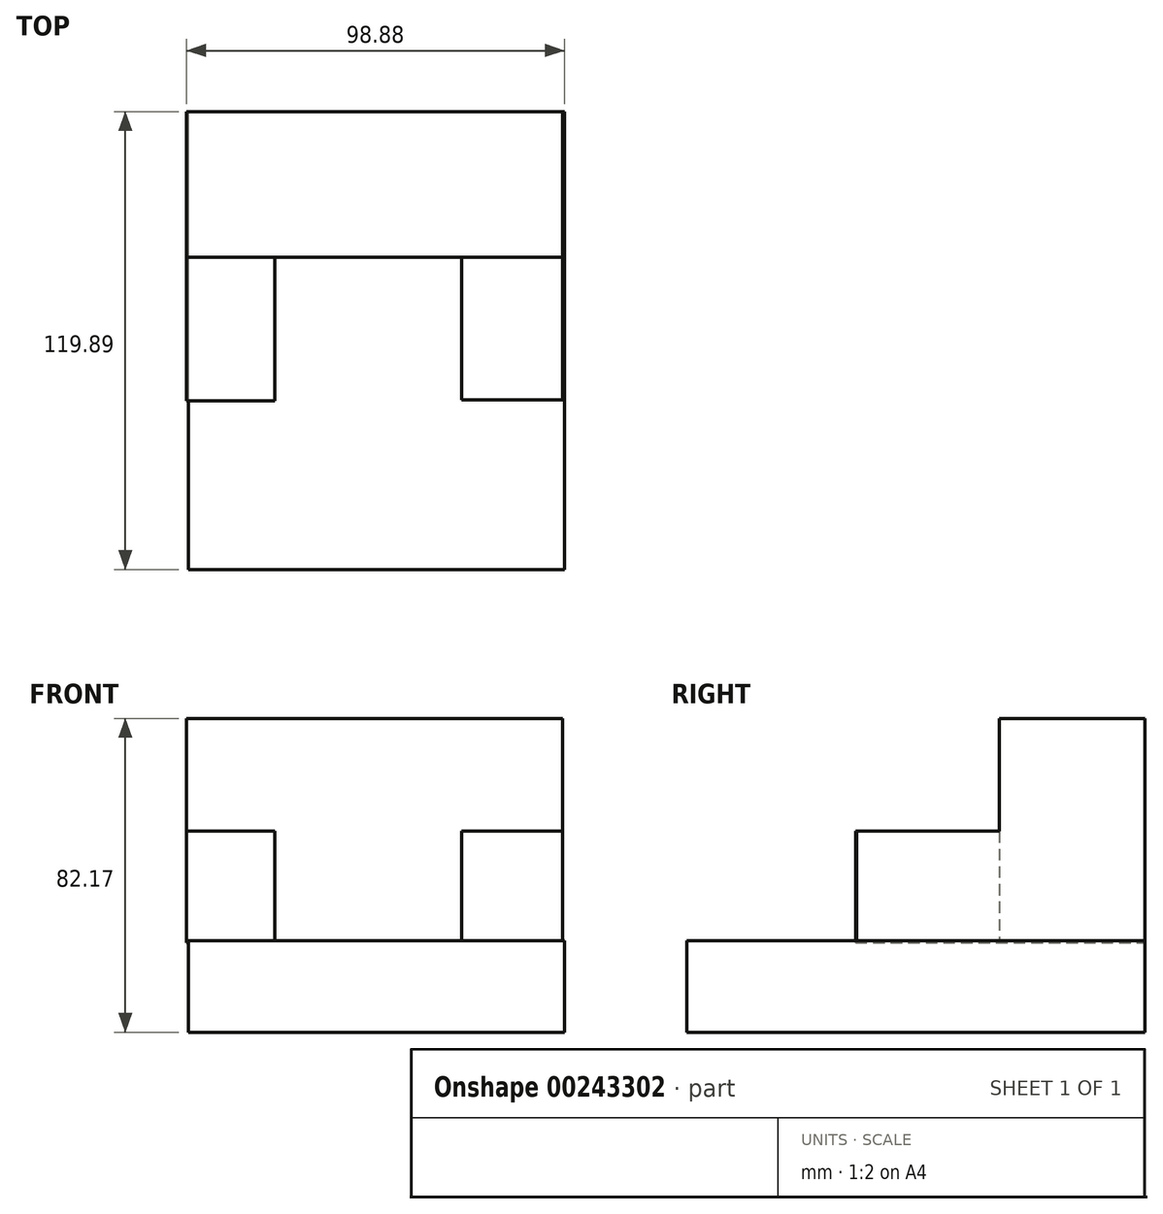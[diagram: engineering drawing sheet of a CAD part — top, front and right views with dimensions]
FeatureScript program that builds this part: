
annotation { "Feature Type Name" : "Feature", "Feature Type Description" : "" }
export const myFeature = defineFeature(function(context is Context, id is Id, definition is map)
    precondition{}
    {
        {
            var Q0;
            Q0=qCreatedBy(makeId("Front.planeOp"),FACE);
            var sketch = newSketch(context, id + "F0", { "sketchPlane" : qUnion([Q0])});
            skLineSegment(sketch, "E0.bottom", {"start": v(-49.67, 29.57) * mm, "end": v(48.76, 29.57) * mm});
            skLineSegment(sketch, "E0.top", {"start": v(-49.67, -29.12) * mm, "end": v(48.76, -29.12) * mm});
            skLineSegment(sketch, "E0.left", {"start": v(-49.67, 29.57) * mm, "end": v(-49.67, -29.12) * mm});
            skLineSegment(sketch, "E0.right", {"start": v(48.76, 29.57) * mm, "end": v(48.76, -29.12) * mm});
            skPoint(sketch, "E0.middle", {"position": v(-0.45, 0.23) * mm});
            skSolve(sketch);
        }
        {
            var Q0;
            Q0=makeQuery(id+"F0.imprint","IMPRINT",FACE,{"disambiguationData":[TD([[makeQuery(id+"F0.imprint","IMPRINT",EDGE,{"derivedFrom":sQuery(id+"F0.wireOp",EDGE,"E0.bottom")}),-1.0]])]});
            extrude(context, id + "F1", {"entities" : qUnion([Q0]), "depth" : 38.1 * mm});
        }
        {
            var Q0;
            Q0=makeQuery(id+"F1.opExtrude","CAP_FACE",FACE,{"disambiguationData":[OSD([sQuery(id+"F0.wireOp",EDGE,"E0.bottom"),sQuery(id+"F0.wireOp",EDGE,"E0.top"),sQuery(id+"F0.wireOp",EDGE,"E0.left"),sQuery(id+"F0.wireOp",EDGE,"E0.right")])],"isStart":false});
            var sketch = newSketch(context, id + "F2", { "sketchPlane" : qUnion([Q0])});
            skPoint(sketch, "E1.firstSnap0", {"position": v(-49.67, 0.23) * mm});
            skLineSegment(sketch, "E1.bottom", {"start": v(-49.67, 0) * mm, "end": v(-26.64, 0) * mm});
            skLineSegment(sketch, "E1.top", {"start": v(-49.67, -29.12) * mm, "end": v(-26.64, -29.12) * mm});
            skLineSegment(sketch, "E1.left", {"start": v(-49.67, 0) * mm, "end": v(-49.67, -29.12) * mm});
            skLineSegment(sketch, "E1.right", {"start": v(-26.64, 0) * mm, "end": v(-26.64, -29.12) * mm});
            skSolve(sketch);
        }
        {
            var Q0;
            Q0=makeQuery(id+"F2.imprint","IMPRINT",FACE,{"disambiguationData":[TD([[makeQuery(id+"F2.imprint","IMPRINT",EDGE,{"derivedFrom":sQuery(id+"F2.wireOp",EDGE,"E1.bottom")}),-1.0]])]});
            extrude(context, id + "F3", {"entities" : qUnion([Q0]), "operationType" : NewBodyOperationType.ADD, "depth" : 37.6 * mm});
        }
        {
            var Q0;
            Q0=makeQuery(id+"F1.opExtrude","CAP_FACE",FACE,{"disambiguationData":[OSD([sQuery(id+"F0.wireOp",EDGE,"E0.bottom"),sQuery(id+"F0.wireOp",EDGE,"E0.top"),sQuery(id+"F0.wireOp",EDGE,"E0.left"),sQuery(id+"F0.wireOp",EDGE,"E0.right")])],"isStart":false});
            var sketch = newSketch(context, id + "F4", { "sketchPlane" : qUnion([Q0])});
            skLineSegment(sketch, "E2.bottom", {"start": v(48.76, 0) * mm, "end": v(22.36, 0) * mm});
            skLineSegment(sketch, "E2.top", {"start": v(48.76, -29.12) * mm, "end": v(22.36, -29.12) * mm});
            skLineSegment(sketch, "E2.left", {"start": v(48.76, 0) * mm, "end": v(48.76, -29.12) * mm});
            skLineSegment(sketch, "E2.right", {"start": v(22.36, 0) * mm, "end": v(22.36, -29.12) * mm});
            skSolve(sketch);
        }
        {
            var Q0;
            Q0=makeQuery(id+"F4.imprint","IMPRINT",FACE,{"disambiguationData":[TD([[makeQuery(id+"F4.imprint","IMPRINT",EDGE,{"derivedFrom":sQuery(id+"F4.wireOp",EDGE,"E2.bottom")}),1.0]])]});
            extrude(context, id + "F5", {"entities" : qUnion([Q0]), "operationType" : NewBodyOperationType.ADD, "depth" : 37.34 * mm});
        }
        {
            var Q0;
            Q0=qCreatedBy(makeId("Front.planeOp"),FACE);
            var sketch = newSketch(context, id + "F6", { "sketchPlane" : qUnion([Q0])});
            skLineSegment(sketch, "E3.bottom", {"start": v(-49.21, -28.67) * mm, "end": v(49.21, -28.67) * mm});
            skLineSegment(sketch, "E3.top", {"start": v(-49.21, -52.6) * mm, "end": v(49.21, -52.6) * mm});
            skLineSegment(sketch, "E3.left", {"start": v(-49.21, -28.67) * mm, "end": v(-49.21, -52.6) * mm});
            skLineSegment(sketch, "E3.right", {"start": v(49.21, -28.67) * mm, "end": v(49.21, -52.6) * mm});
            skSolve(sketch);
        }
        {
            var Q0;
            Q0=makeQuery(id+"F6.imprint","IMPRINT",FACE,{"disambiguationData":[TD([[makeQuery(id+"F6.imprint","IMPRINT",EDGE,{"derivedFrom":sQuery(id+"F6.wireOp",EDGE,"E3.bottom")}),-1.0]])]});
            extrude(context, id + "F7", {"entities" : qUnion([Q0]), "operationType" : NewBodyOperationType.ADD, "depth" : 119.89 * mm});
        }
    });
